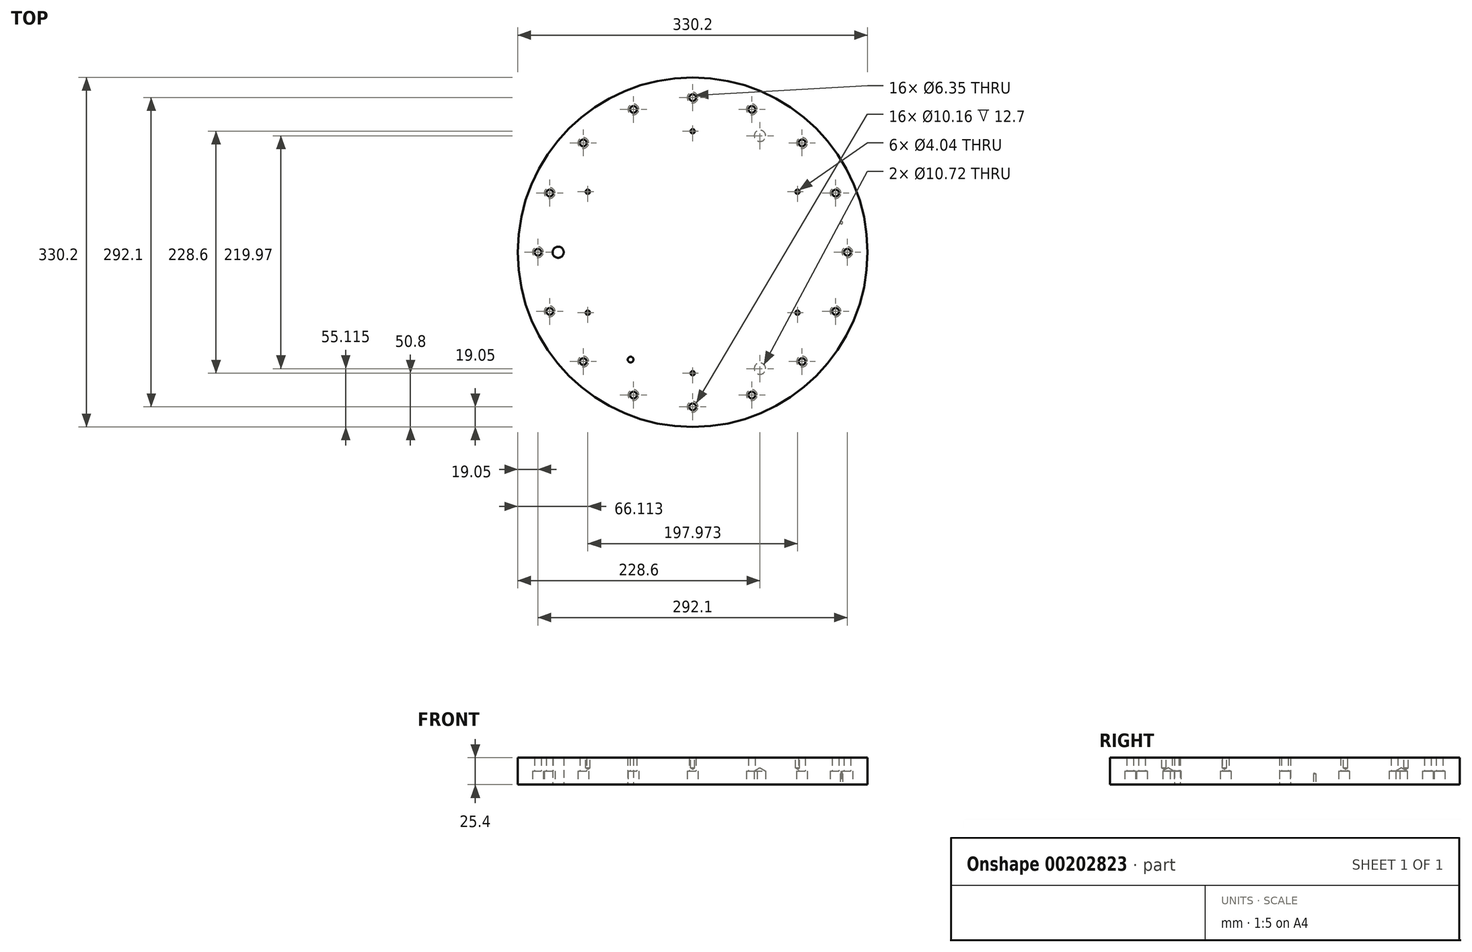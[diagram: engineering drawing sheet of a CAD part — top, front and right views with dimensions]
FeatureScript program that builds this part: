
annotation { "Feature Type Name" : "Feature", "Feature Type Description" : "" }
export const myFeature = defineFeature(function(context is Context, id is Id, definition is map)
    precondition{}
    {
        {
            var Q0;
            Q0=qCreatedBy(makeId("Top.planeOp"),FACE);
            var sketch = newSketch(context, id + "F0", { "sketchPlane" : qUnion([Q0])});
            skCircle(sketch, "E0", {"center": v(0, 0) * mm, "radius": 165.1 * mm});
            skSolve(sketch);
        }
        {
            var Q0;
            Q0 = qSketchRegion(id + "F0", true);
            extrude(context, id + "F1", {"entities" : qUnion([Q0]), "oppositeDirection" : true, "depth" : 25.4 * mm});
        }
        {
            var Q0;
            Q0=makeQuery(id+"F1.opExtrude","CAP_FACE",FACE,{"disambiguationData":[OSD([sQuery(id+"F0.wireOp",EDGE,"E0")])],"isStart":true});
            var sketch = newSketch(context, id + "F2", { "sketchPlane" : qUnion([Q0])});
            skCircle(sketch, "E1", {"center": v(0, 0) * mm, "radius": 114.3 * mm, "construction": true});
            skPoint(sketch, "E2", {"position": v(0, 114.3) * mm});
            skPoint(sketch, "E3.1.0", {"position": v(-98.99, 57.15) * mm});
            skPoint(sketch, "E3.2.0", {"position": v(-98.99, -57.15) * mm});
            skPoint(sketch, "E3.3.0", {"position": v(0, -114.3) * mm});
            skPoint(sketch, "E3.4.0", {"position": v(98.99, -57.15) * mm});
            skPoint(sketch, "E3.5.0", {"position": v(98.99, 57.15) * mm});
            skSolve(sketch);
        }
        {
            var Q0;
            Q0=sQuery(id+"F2.wireOp",VERTEX,"E3.1.0");
            var Q1;
            Q1=sQuery(id+"F2.wireOp",VERTEX,"E3.2.0");
            var Q2;
            Q2=sQuery(id+"F2.wireOp",VERTEX,"E3.3.0");
            var Q3;
            Q3=sQuery(id+"F2.wireOp",VERTEX,"E3.4.0");
            var Q4;
            Q4=sQuery(id+"F2.wireOp",VERTEX,"E3.5.0");
            var Q5;
            Q5=sQuery(id+"F2.wireOp",VERTEX,"E2");
            var Q6;
            Q6=makeQuery(id+"F1.opExtrude","SWEPT_BODY",BODY,{"disambiguationData":[OSD([sQuery(id+"F0.wireOp",EDGE,"E0")])]});
            hole(context, id + "F3", {"style" : HoleStyle.SIMPLE, "endStyle" : HoleEndStyle.BLIND, "standardTappedOrClearance" : lookupTablePath({ "standard" : "ANSI", "engagement" : "75%", "pitch" : "32 tpi", "size" : "#10", "type" : "Tapped" }), "standardBlindInLast" : lookupTablePath({ "standard" : "ANSI", "engagement" : "75%", "pitch" : "32 tpi", "size" : "#10", "type" : "Tapped" }), "holeDiameter" : 4.04 * mm, "holeDepth" : 9.65 * mm, "startFromSketch" : true, "locations" : qUnion([Q0, Q1, Q2, Q3, Q4, Q5]), "scope" : qUnion([Q6]), "majorDiameter" : 4.83 * mm});
        }
        {
            var Q0;
            Q0=makeQuery(id+"F1.opExtrude","CAP_FACE",FACE,{"disambiguationData":[OSD([sQuery(id+"F0.wireOp",EDGE,"E0")])],"isStart":false});
            var sketch = newSketch(context, id + "F4", { "sketchPlane" : qUnion([Q0])});
            skPoint(sketch, "E4", {"position": v(-58.58, 101.46) * mm});
            skPoint(sketch, "E5", {"position": v(-127, 0) * mm});
            skPoint(sketch, "E6", {"position": v(140.46, -27.94) * mm});
            skPoint(sketch, "E7.1.0", {"position": v(63.5, -109.99) * mm});
            skPoint(sketch, "E7.2.0", {"position": v(63.5, 109.99) * mm});
            skPoint(sketch, "E7.center", {"position": v(0, 0) * mm});
            skCircle(sketch, "E8", {"center": v(0, 0) * mm, "radius": 146.05 * mm, "construction": true});
            skPoint(sketch, "E9", {"position": v(-146.05, 0) * mm});
            skPoint(sketch, "E10.1.0", {"position": v(-134.93, -55.9) * mm});
            skPoint(sketch, "E10.2.0", {"position": v(-103.27, -103.27) * mm});
            skPoint(sketch, "E10.3.0", {"position": v(-55.9, -134.93) * mm});
            skPoint(sketch, "E10.4.0", {"position": v(0, -146.05) * mm});
            skPoint(sketch, "E10.5.0", {"position": v(55.9, -134.93) * mm});
            skPoint(sketch, "E10.6.0", {"position": v(103.27, -103.27) * mm});
            skPoint(sketch, "E10.7.0", {"position": v(134.93, -55.9) * mm});
            skPoint(sketch, "E10.8.0", {"position": v(146.05, 0) * mm});
            skPoint(sketch, "E10.9.0", {"position": v(134.93, 55.9) * mm});
            skPoint(sketch, "E10.10.0", {"position": v(103.27, 103.27) * mm});
            skPoint(sketch, "E10.11.0", {"position": v(55.9, 134.93) * mm});
            skPoint(sketch, "E10.12.0", {"position": v(0, 146.05) * mm});
            skPoint(sketch, "E10.13.0", {"position": v(-55.9, 134.93) * mm});
            skPoint(sketch, "E10.14.0", {"position": v(-103.27, 103.27) * mm});
            skPoint(sketch, "E10.15.0", {"position": v(-134.93, 55.9) * mm});
            skSolve(sketch);
        }
        {
            var Q0;
            Q0=sQuery(id+"F4.wireOp",VERTEX,"E10.15.0");
            var Q1;
            Q1=sQuery(id+"F4.wireOp",VERTEX,"E10.14.0");
            var Q2;
            Q2=sQuery(id+"F4.wireOp",VERTEX,"E10.13.0");
            var Q3;
            Q3=sQuery(id+"F4.wireOp",VERTEX,"E10.12.0");
            var Q4;
            Q4=sQuery(id+"F4.wireOp",VERTEX,"E10.11.0");
            var Q5;
            Q5=sQuery(id+"F4.wireOp",VERTEX,"E10.10.0");
            var Q6;
            Q6=sQuery(id+"F4.wireOp",VERTEX,"E10.9.0");
            var Q7;
            Q7=sQuery(id+"F4.wireOp",VERTEX,"E10.8.0");
            var Q8;
            Q8=sQuery(id+"F4.wireOp",VERTEX,"E10.7.0");
            var Q9;
            Q9=sQuery(id+"F4.wireOp",VERTEX,"E10.6.0");
            var Q10;
            Q10=sQuery(id+"F4.wireOp",VERTEX,"E10.5.0");
            var Q11;
            Q11=sQuery(id+"F4.wireOp",VERTEX,"E10.4.0");
            var Q12;
            Q12=sQuery(id+"F4.wireOp",VERTEX,"E10.3.0");
            var Q13;
            Q13=sQuery(id+"F4.wireOp",VERTEX,"E10.2.0");
            var Q14;
            Q14=sQuery(id+"F4.wireOp",VERTEX,"E10.1.0");
            var Q15;
            Q15=sQuery(id+"F4.wireOp",VERTEX,"E9");
            var Q16;
            Q16=makeQuery(id+"F1.opExtrude","SWEPT_BODY",BODY,{"disambiguationData":[OSD([sQuery(id+"F0.wireOp",EDGE,"E0")])]});
            hole(context, id + "F5", {"style" : HoleStyle.C_BORE, "endStyle" : HoleEndStyle.THROUGH, "holeDiameter" : 6.35 * mm, "cBoreDiameter" : 10.16 * mm, "cBoreDepth" : 12.7 * mm, "startFromSketch" : true, "locations" : qUnion([Q0, Q1, Q2, Q3, Q4, Q5, Q6, Q7, Q8, Q9, Q10, Q11, Q12, Q13, Q14, Q15]), "scope" : qUnion([Q16]), "isTappedThrough" : true});
        }
        {
            var Q0;
            Q0=sQuery(id+"F4.wireOp",VERTEX,"E5");
            var Q1;
            Q1=makeQuery(id+"F1.opExtrude","SWEPT_BODY",BODY,{"disambiguationData":[OSD([sQuery(id+"F0.wireOp",EDGE,"E0")])]});
            hole(context, id + "F6", {"style" : HoleStyle.SIMPLE, "endStyle" : HoleEndStyle.THROUGH, "standardTappedOrClearance" : lookupTablePath({ "standard" : "ISO", "engagement" : "75%", "pitch" : "1.5 mm", "size" : "M12", "type" : "Tapped" }), "standardBlindInLast" : lookupTablePath({ "standard" : "ISO", "engagement" : "75%", "pitch" : "1.5 mm", "size" : "M12", "type" : "Tapped" }), "holeDiameter" : 10.5 * mm, "startFromSketch" : true, "locations" : qUnion([Q0]), "scope" : qUnion([Q1]), "isTappedThrough" : true, "majorDiameter" : 12 * mm, "showTappedDepth" : true});
        }
        {
            var Q0;
            Q0=sQuery(id+"F4.wireOp",VERTEX,"E6");
            var Q1;
            Q1=makeQuery(id+"F1.opExtrude","SWEPT_BODY",BODY,{"disambiguationData":[OSD([sQuery(id+"F0.wireOp",EDGE,"E0")])]});
            hole(context, id + "F7", {"style" : HoleStyle.SIMPLE, "endStyle" : HoleEndStyle.BLIND, "standardTappedOrClearance" : lookupTablePath({ "standard" : "ANSI", "engagement" : "75%", "pitch" : "40 tpi", "size" : "#4", "type" : "Tapped" }), "standardBlindInLast" : lookupTablePath({ "standard" : "ANSI", "engagement" : "75%", "pitch" : "40 tpi", "size" : "#4", "type" : "Tapped" }), "holeDiameter" : 2.26 * mm, "holeDepth" : 10.16 * mm, "startFromSketch" : true, "locations" : qUnion([Q0]), "scope" : qUnion([Q1]), "majorDiameter" : 2.84 * mm});
        }
        {
            var Q0;
            Q0=sQuery(id+"F4.wireOp",VERTEX,"E4");
            var Q1;
            Q1=makeQuery(id+"F1.opExtrude","SWEPT_BODY",BODY,{"disambiguationData":[OSD([sQuery(id+"F0.wireOp",EDGE,"E0")])]});
            hole(context, id + "F8", {"style" : HoleStyle.SIMPLE, "endStyle" : HoleEndStyle.THROUGH, "standardTappedOrClearance" : lookupTablePath({ "standard" : "ANSI", "engagement" : "75%", "pitch" : "28 tpi", "size" : "1/4", "type" : "Tapped" }), "standardBlindInLast" : lookupTablePath({ "standard" : "ANSI", "engagement" : "75%", "pitch" : "28 tpi", "size" : "1/4", "type" : "Tapped" }), "holeDiameter" : 5.4 * mm, "startFromSketch" : true, "locations" : qUnion([Q0]), "scope" : qUnion([Q1]), "isTappedThrough" : true, "majorDiameter" : 6.35 * mm, "showTappedDepth" : true});
        }
        {
            var Q0;
            Q0=sQuery(id+"F4.wireOp",VERTEX,"E7.1.0");
            var Q1;
            Q1=sQuery(id+"F4.wireOp",VERTEX,"E7.2.0");
            var Q2;
            Q2=makeQuery(id+"F1.opExtrude","SWEPT_BODY",BODY,{"disambiguationData":[OSD([sQuery(id+"F0.wireOp",EDGE,"E0")])]});
            hole(context, id + "F9", {"style" : HoleStyle.SIMPLE, "endStyle" : HoleEndStyle.BLIND, "standardTappedOrClearance" : lookupTablePath({ "standard" : "ANSI", "engagement" : "75%", "pitch" : "13 tpi", "size" : "1/2", "type" : "Tapped" }), "standardBlindInLast" : lookupTablePath({ "standard" : "ANSI", "engagement" : "75%", "pitch" : "13 tpi", "size" : "1/2", "type" : "Tapped" }), "holeDiameter" : 10.72 * mm, "holeDepth" : 12.7 * mm, "startFromSketch" : true, "locations" : qUnion([Q0, Q1]), "scope" : qUnion([Q2]), "majorDiameter" : 12.7 * mm});
        }
    });
